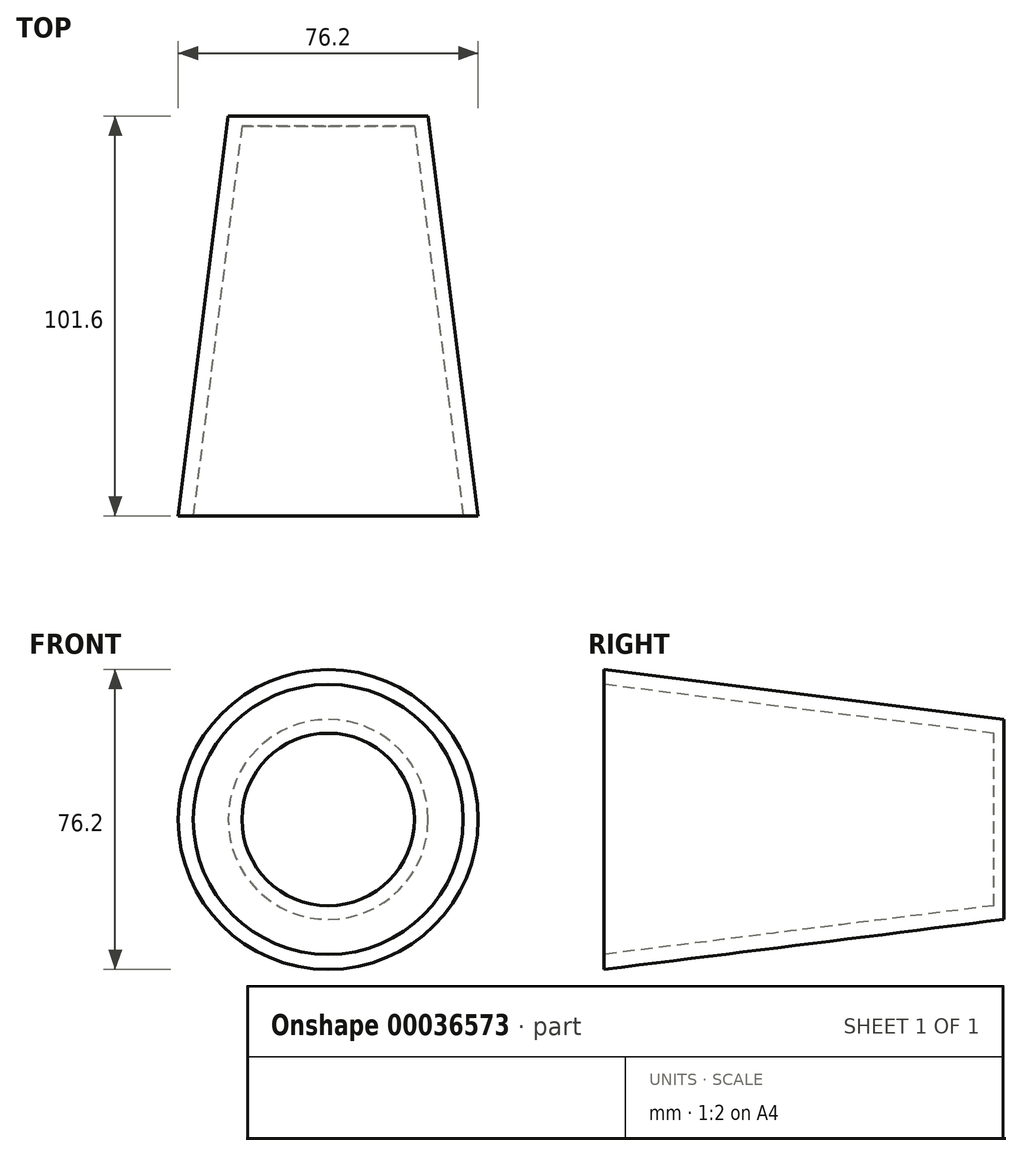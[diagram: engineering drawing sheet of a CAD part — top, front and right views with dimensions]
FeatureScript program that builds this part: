
annotation { "Feature Type Name" : "Feature", "Feature Type Description" : "" }
export const myFeature = defineFeature(function(context is Context, id is Id, definition is map)
    precondition{}
    {
        {
            var Q0;
            Q0=qCreatedBy(makeId("Front.planeOp"),FACE);
            var sketch = newSketch(context, id + "F0", { "sketchPlane" : qUnion([Q0])});
            skCircle(sketch, "E0", {"center": v(0, 0) * mm, "radius": 25.4 * mm});
            skSolve(sketch);
        }
        {
            var Q0;
            Q0=qCreatedBy(makeId("Front.planeOp"),FACE);
            cPlane(context, id + "F1", {"entities" : qUnion([Q0]), "cplaneType" : CPlaneType.OFFSET, "offset" : 101.6 * mm, "width" : 152.4 * mm, "height" : 152.4 * mm});
        }
        {
            var Q0;
            Q0=qCreatedBy(id+"F1.planeOp",FACE);
            var sketch = newSketch(context, id + "F2", { "sketchPlane" : qUnion([Q0])});
            skPoint(sketch, "E1", {"position": v(0, 0) * mm});
            skCircle(sketch, "E2", {"center": v(0, 0) * mm, "radius": 38.1 * mm});
            skSolve(sketch);
        }
        {
            var Q0;
            Q0=makeQuery(id+"F0.imprint","IMPRINT",FACE,{"disambiguationData":[TD([[makeQuery(id+"F0.imprint","IMPRINT",EDGE,{"derivedFrom":sQuery(id+"F0.wireOp",EDGE,"E0")}),1.0]])]});
            var Q1;
            Q1=makeQuery(id+"F2.imprint","IMPRINT",FACE,{"disambiguationData":[TD([[makeQuery(id+"F2.imprint","IMPRINT",EDGE,{"derivedFrom":sQuery(id+"F2.wireOp",EDGE,"E2")}),1.0]])]});
            loft(context, id + "F3", {"sheetProfilesArray" : [{ "sheetProfileEntities" : qUnion([Q0]) }, { "sheetProfileEntities" : qUnion([Q1]) }]});
        }
        {
            var Q0;
            Q0=makeQuery(id+"F3.opLoft","CAP_FACE",FACE,{"disambiguationData":[OSD([makeQuery(id+"F2.imprint","IMPRINT",FACE,{"disambiguationData":[TD([[makeQuery(id+"F2.imprint","IMPRINT",EDGE,{"derivedFrom":sQuery(id+"F2.wireOp",EDGE,"E2")}),1.0]])]})])],"isStart":true});
            var sketch = newSketch(context, id + "F4", { "sketchPlane" : qUnion([Q0])});
            skCircle(sketch, "E3", {"center": v(0, 0) * mm, "radius": 34.3 * mm});
            skSolve(sketch);
        }
        {
            var Q0;
            Q0=makeQuery(id+"F3.opLoft","CAP_FACE",FACE,{"disambiguationData":[OSD([makeQuery(id+"F0.imprint","IMPRINT",FACE,{"disambiguationData":[TD([[makeQuery(id+"F0.imprint","IMPRINT",EDGE,{"derivedFrom":sQuery(id+"F0.wireOp",EDGE,"E0")}),1.0]])]})])],"isStart":true});
            var sketch = newSketch(context, id + "F5", { "sketchPlane" : qUnion([Q0])});
            skCircle(sketch, "E4", {"center": v(0, 0) * mm, "radius": 21.6 * mm});
            skSolve(sketch);
        }
        {
            var Q1;
            Q1=makeQuery(id+"F5.imprint","IMPRINT",FACE,{"disambiguationData":[TD([[makeQuery(id+"F5.imprint","IMPRINT",EDGE,{"derivedFrom":sQuery(id+"F5.wireOp",EDGE,"E4")}),1.0]])]});
            var Q2;
            Q2=makeQuery(id+"F4.imprint","IMPRINT",FACE,{"disambiguationData":[TD([[makeQuery(id+"F4.imprint","IMPRINT",EDGE,{"derivedFrom":sQuery(id+"F4.wireOp",EDGE,"E3")}),1.0]])]});
            loft(context, id + "F6", {"operationType" : NewBodyOperationType.REMOVE, "sheetProfilesArray" : [{ "sheetProfileEntities" : qUnion([Q1]) }, { "sheetProfileEntities" : qUnion([Q2]) }]});
        }
        {
            var Q0;
            Q0=qCreatedBy(makeId("Front.planeOp"),FACE);
            var sketch = newSketch(context, id + "F7", { "sketchPlane" : qUnion([Q0])});
            skCircle(sketch, "E5", {"center": v(0, 0) * mm, "radius": 24.97 * mm});
            skSolve(sketch);
        }
        {
            var Q0;
            Q0 = qSketchRegion(id + "F7", true);
            extrude(context, id + "F8", {"entities" : qUnion([Q0]), "operationType" : NewBodyOperationType.ADD, "depth" : 2.54 * mm});
        }
    });
